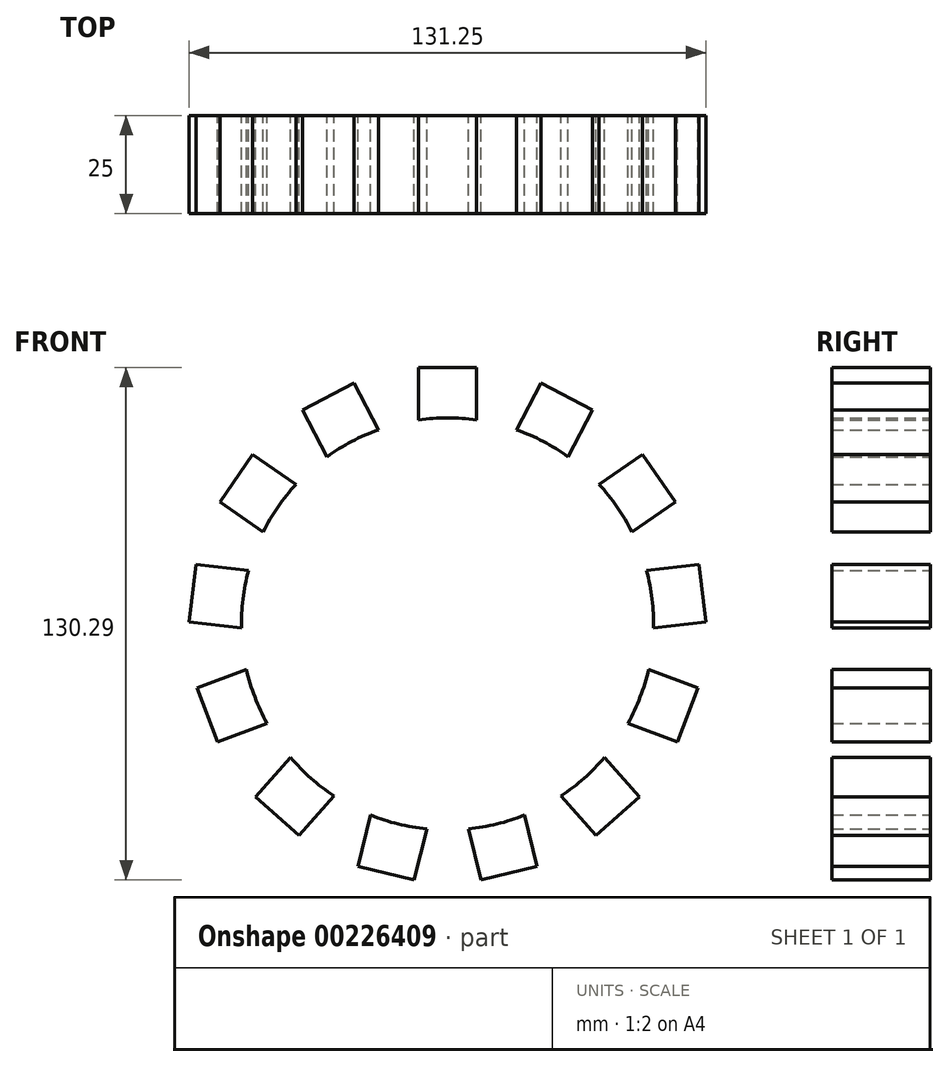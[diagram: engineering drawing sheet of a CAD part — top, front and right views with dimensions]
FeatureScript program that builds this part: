
annotation { "Feature Type Name" : "Feature", "Feature Type Description" : "" }
export const myFeature = defineFeature(function(context is Context, id is Id, definition is map)
    precondition{}
    {
        {
            var Q0;
            Q0=qCreatedBy(makeId("Front.planeOp"),FACE);
            var sketch = newSketch(context, id + "F0", { "sketchPlane" : qUnion([Q0])});
            skCircle(sketch, "E0", {"center": v(-15.16, -13.53) * mm, "radius": 52.35 * mm});
            skLineSegment(sketch, "E1", {"start": v(-15.16, -13.53) * mm, "end": v(-15.16, 91.18) * mm, "construction": true});
            skLineSegment(sketch, "E2", {"start": v(-22.5, 38.3) * mm, "end": v(-22.5, 51.68) * mm});
            skLineSegment(sketch, "E3", {"start": v(-22.5, 51.68) * mm, "end": v(-7.81, 51.68) * mm});
            skLineSegment(sketch, "E4", {"start": v(-7.81, 51.68) * mm, "end": v(-7.81, 38.3) * mm});
            skPoint(sketch, "E5", {"position": v(-15.16, 38.82) * mm});
            skLineSegment(sketch, "E6.1.0", {"start": v(-38.96, 47.63) * mm, "end": v(-32.74, 35.78) * mm});
            skLineSegment(sketch, "E6.1.1", {"start": v(-51.97, 40.8) * mm, "end": v(-38.96, 47.63) * mm});
            skLineSegment(sketch, "E6.1.2", {"start": v(-45.75, 28.95) * mm, "end": v(-51.97, 40.8) * mm});
            skLineSegment(sketch, "E6.2.0", {"start": v(-64.66, 29.56) * mm, "end": v(-53.64, 21.96) * mm});
            skLineSegment(sketch, "E6.2.1", {"start": v(-73, 17.47) * mm, "end": v(-64.66, 29.56) * mm});
            skLineSegment(sketch, "E6.2.2", {"start": v(-62, 9.87) * mm, "end": v(-73, 17.47) * mm});
            skLineSegment(sketch, "E6.3.0", {"start": v(-79.01, 1.62) * mm, "end": v(-65.73, 0.01) * mm});
            skLineSegment(sketch, "E6.3.1", {"start": v(-80.78, -12.96) * mm, "end": v(-79.01, 1.62) * mm});
            skLineSegment(sketch, "E6.3.2", {"start": v(-67.5, -14.58) * mm, "end": v(-80.78, -12.96) * mm});
            skLineSegment(sketch, "E6.4.0", {"start": v(-78.74, -29.79) * mm, "end": v(-66.23, -25.04) * mm});
            skLineSegment(sketch, "E6.4.1", {"start": v(-73.53, -43.53) * mm, "end": v(-78.74, -29.79) * mm});
            skLineSegment(sketch, "E6.4.2", {"start": v(-61.02, -38.78) * mm, "end": v(-73.53, -43.53) * mm});
            skLineSegment(sketch, "E6.5.0", {"start": v(-63.9, -57.47) * mm, "end": v(-55.03, -47.46) * mm});
            skLineSegment(sketch, "E6.5.1", {"start": v(-52.9, -67.22) * mm, "end": v(-63.9, -57.47) * mm});
            skLineSegment(sketch, "E6.5.2", {"start": v(-44.03, -57.2) * mm, "end": v(-52.9, -67.22) * mm});
            skLineSegment(sketch, "E6.6.0", {"start": v(-37.9, -75.1) * mm, "end": v(-34.7, -62.1) * mm});
            skLineSegment(sketch, "E6.6.1", {"start": v(-23.63, -78.6) * mm, "end": v(-37.9, -75.1) * mm});
            skLineSegment(sketch, "E6.6.2", {"start": v(-20.43, -65.62) * mm, "end": v(-23.63, -78.6) * mm});
            skLineSegment(sketch, "E6.7.0", {"start": v(-6.69, -78.6) * mm, "end": v(-9.89, -65.62) * mm});
            skLineSegment(sketch, "E6.7.1", {"start": v(7.58, -75.1) * mm, "end": v(-6.69, -78.6) * mm});
            skLineSegment(sketch, "E6.7.2", {"start": v(4.38, -62.1) * mm, "end": v(7.58, -75.1) * mm});
            skLineSegment(sketch, "E6.8.0", {"start": v(22.59, -67.22) * mm, "end": v(13.72, -57.2) * mm});
            skLineSegment(sketch, "E6.8.1", {"start": v(33.59, -57.47) * mm, "end": v(22.59, -67.22) * mm});
            skLineSegment(sketch, "E6.8.2", {"start": v(24.72, -47.46) * mm, "end": v(33.59, -57.47) * mm});
            skLineSegment(sketch, "E6.9.0", {"start": v(43.21, -43.53) * mm, "end": v(30.7, -38.78) * mm});
            skLineSegment(sketch, "E6.9.1", {"start": v(48.42, -29.79) * mm, "end": v(43.21, -43.53) * mm});
            skLineSegment(sketch, "E6.9.2", {"start": v(35.91, -25.04) * mm, "end": v(48.42, -29.79) * mm});
            skLineSegment(sketch, "E6.10.0", {"start": v(50.47, -12.96) * mm, "end": v(37.19, -14.58) * mm});
            skLineSegment(sketch, "E6.10.1", {"start": v(48.7, 1.62) * mm, "end": v(50.47, -12.96) * mm});
            skLineSegment(sketch, "E6.10.2", {"start": v(35.41, 0.01) * mm, "end": v(48.7, 1.62) * mm});
            skLineSegment(sketch, "E6.11.0", {"start": v(42.69, 17.47) * mm, "end": v(31.68, 9.87) * mm});
            skLineSegment(sketch, "E6.11.1", {"start": v(34.34, 29.56) * mm, "end": v(42.69, 17.47) * mm});
            skLineSegment(sketch, "E6.11.2", {"start": v(23.33, 21.96) * mm, "end": v(34.34, 29.56) * mm});
            skLineSegment(sketch, "E6.12.0", {"start": v(21.65, 40.8) * mm, "end": v(15.44, 28.95) * mm});
            skLineSegment(sketch, "E6.12.1", {"start": v(8.64, 47.63) * mm, "end": v(21.65, 40.8) * mm});
            skLineSegment(sketch, "E6.12.2", {"start": v(2.43, 35.78) * mm, "end": v(8.64, 47.63) * mm});
            skCircle(sketch, "E7", {"center": v(-15.16, -13.53) * mm, "radius": 22.33 * mm});
            skSolve(sketch);
        }
        {
            var Q0;
            {var subQ0=sQuery(id+"F0.wireOp",EDGE,"E6.11.0");Q0=makeQuery(id+"F0.imprint","IMPRINT",FACE,{"disambiguationData":[TD([[makeQuery(id+"F0.imprint","IMPRINT",EDGE,{"derivedFrom":subQ0}),-1.0]])]});}
            var Q1;
            {var subQ0=sQuery(id+"F0.wireOp",EDGE,"E6.12.0");Q1=makeQuery(id+"F0.imprint","IMPRINT",FACE,{"disambiguationData":[TD([[makeQuery(id+"F0.imprint","IMPRINT",EDGE,{"derivedFrom":subQ0}),-1.0]])]});}
            var Q2;
            {var subQ0=sQuery(id+"F0.wireOp",EDGE,"E2");Q2=makeQuery(id+"F0.imprint","IMPRINT",FACE,{"disambiguationData":[TD([[makeQuery(id+"F0.imprint","IMPRINT",EDGE,{"derivedFrom":subQ0}),-1.0]])]});}
            var Q3;
            {var subQ0=sQuery(id+"F0.wireOp",EDGE,"E6.1.0");Q3=makeQuery(id+"F0.imprint","IMPRINT",FACE,{"disambiguationData":[TD([[makeQuery(id+"F0.imprint","IMPRINT",EDGE,{"derivedFrom":subQ0}),-1.0]])]});}
            var Q4;
            {var subQ0=sQuery(id+"F0.wireOp",EDGE,"E6.2.0");Q4=makeQuery(id+"F0.imprint","IMPRINT",FACE,{"disambiguationData":[TD([[makeQuery(id+"F0.imprint","IMPRINT",EDGE,{"derivedFrom":subQ0}),-1.0]])]});}
            var Q5;
            {var subQ0=sQuery(id+"F0.wireOp",EDGE,"E6.3.0");Q5=makeQuery(id+"F0.imprint","IMPRINT",FACE,{"disambiguationData":[TD([[makeQuery(id+"F0.imprint","IMPRINT",EDGE,{"derivedFrom":subQ0}),-1.0]])]});}
            var Q6;
            {var subQ0=sQuery(id+"F0.wireOp",EDGE,"E6.4.0");Q6=makeQuery(id+"F0.imprint","IMPRINT",FACE,{"disambiguationData":[TD([[makeQuery(id+"F0.imprint","IMPRINT",EDGE,{"derivedFrom":subQ0}),-1.0]])]});}
            var Q7;
            {var subQ0=sQuery(id+"F0.wireOp",EDGE,"E6.5.0");Q7=makeQuery(id+"F0.imprint","IMPRINT",FACE,{"disambiguationData":[TD([[makeQuery(id+"F0.imprint","IMPRINT",EDGE,{"derivedFrom":subQ0}),-1.0]])]});}
            var Q8;
            {var subQ0=sQuery(id+"F0.wireOp",EDGE,"E6.6.0");Q8=makeQuery(id+"F0.imprint","IMPRINT",FACE,{"disambiguationData":[TD([[makeQuery(id+"F0.imprint","IMPRINT",EDGE,{"derivedFrom":subQ0}),-1.0]])]});}
            var Q9;
            {var subQ0=sQuery(id+"F0.wireOp",EDGE,"E6.7.0");Q9=makeQuery(id+"F0.imprint","IMPRINT",FACE,{"disambiguationData":[TD([[makeQuery(id+"F0.imprint","IMPRINT",EDGE,{"derivedFrom":subQ0}),-1.0]])]});}
            var Q10;
            {var subQ0=sQuery(id+"F0.wireOp",EDGE,"E6.8.0");Q10=makeQuery(id+"F0.imprint","IMPRINT",FACE,{"disambiguationData":[TD([[makeQuery(id+"F0.imprint","IMPRINT",EDGE,{"derivedFrom":subQ0}),-1.0]])]});}
            var Q11;
            {var subQ0=sQuery(id+"F0.wireOp",EDGE,"E6.9.0");Q11=makeQuery(id+"F0.imprint","IMPRINT",FACE,{"disambiguationData":[TD([[makeQuery(id+"F0.imprint","IMPRINT",EDGE,{"derivedFrom":subQ0}),-1.0]])]});}
            var Q12;
            {var subQ0=sQuery(id+"F0.wireOp",EDGE,"E6.10.0");Q12=makeQuery(id+"F0.imprint","IMPRINT",FACE,{"disambiguationData":[TD([[makeQuery(id+"F0.imprint","IMPRINT",EDGE,{"derivedFrom":subQ0}),-1.0]])]});}
            extrude(context, id + "F1", {"entities" : qUnion([Q0, Q1, Q2, Q3, Q4, Q5, Q6, Q7, Q8, Q9, Q10, Q11, Q12]), "depth" : 25 * mm});
        }
    });
